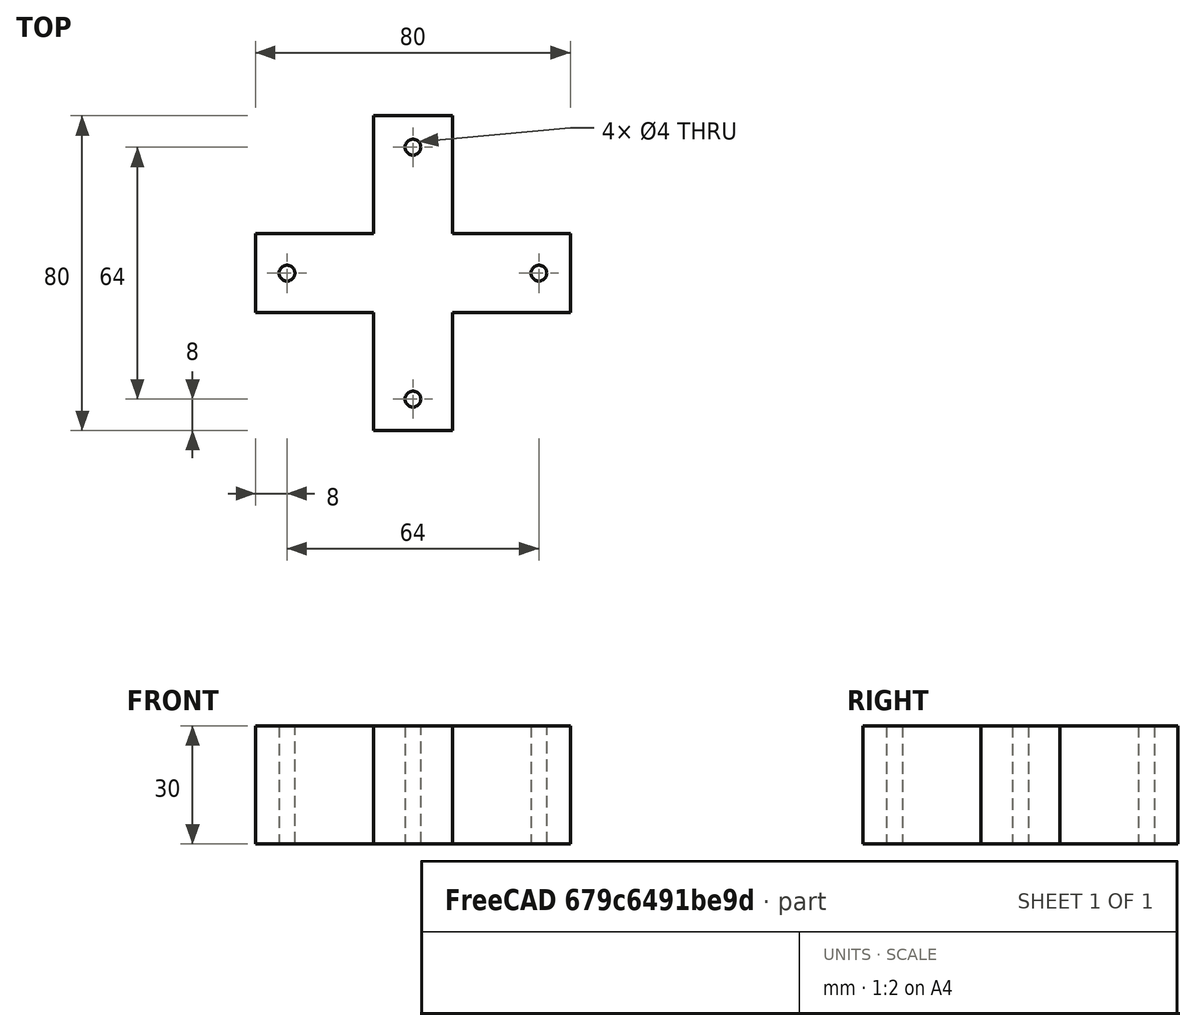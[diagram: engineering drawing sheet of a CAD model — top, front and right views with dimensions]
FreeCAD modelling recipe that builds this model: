
FCSTD DOCUMENT  (FreeCAD 0.21R33694 (Git))
Label: OJT1_T018_Creu
License: All rights reserved
LicenseURL: https://en.wikipedia.org/wiki/All_rights_reserved
objects: Sketcher::SketchObject×1, PartDesign::Pad×1, PartDesign::Body×1
note: 4 computed .brp shape members not serialized (recipe doc carries the construction recipe); baked Part::Feature solids carry a one-line shape summary decoded from their .brp

FEATURE [Sketcher::SketchObject] Sketch
  FullyConstrained = false
  MapMode = 5
  Support = -> [XY_Plane]
  sketch-geometry (16):
    g0: LineSegment StartX=-10 StartY=10 StartZ=0 EndX=-10 EndY=40 EndZ=0
    g1: LineSegment StartX=-10 StartY=40 StartZ=0 EndX=10 EndY=40 EndZ=0
    g2: LineSegment StartX=10 StartY=40 StartZ=0 EndX=10 EndY=10 EndZ=0
    g3: LineSegment StartX=10 StartY=10 StartZ=0 EndX=40 EndY=10 EndZ=0
    g4: LineSegment StartX=40 StartY=10 StartZ=0 EndX=40 EndY=-10 EndZ=0
    g5: LineSegment StartX=40 StartY=-10 StartZ=0 EndX=10 EndY=-10 EndZ=0
    g6: LineSegment StartX=10 StartY=-10 StartZ=0 EndX=10 EndY=-40 EndZ=0
    g7: LineSegment StartX=10 StartY=-40 StartZ=0 EndX=-10 EndY=-40 EndZ=0
    g8: LineSegment StartX=-10 StartY=-40 StartZ=0 EndX=-10 EndY=-10 EndZ=0
    g9: LineSegment StartX=-10 StartY=-10 StartZ=0 EndX=-40 EndY=-10 EndZ=0
    g10: LineSegment StartX=-40 StartY=-10 StartZ=0 EndX=-40 EndY=10 EndZ=0
    g11: LineSegment StartX=-40 StartY=10 StartZ=0 EndX=-10 EndY=10 EndZ=0
    g12: Circle CenterX=-32 CenterY=-3e-16 CenterZ=0 NormalX=0 NormalY=0 NormalZ=1 AngleXU=0 Radius=2
    g13: Circle CenterX=-4e-16 CenterY=-32 CenterZ=0 NormalX=0 NormalY=0 NormalZ=1 AngleXU=0 Radius=2
    g14: Circle CenterX=32 CenterY=-3e-16 CenterZ=0 NormalX=0 NormalY=0 NormalZ=1 AngleXU=0 Radius=2
    g15: Circle CenterX=-4e-16 CenterY=32 CenterZ=0 NormalX=0 NormalY=0 NormalZ=1 AngleXU=0 Radius=2
  constraints (39):
    c: Vertical(g0)
    c: Coincident(g0,g1)
    c: Horizontal(g1)
    c: Coincident(g1,g2)
    c: Vertical(g2)
    c: Coincident(g2,g3)
    c: Horizontal(g3)
    c: Coincident(g3,g4)
    c: Vertical(g4)
    c: Coincident(g4,g5)
    c: Horizontal(g5)
    c: Coincident(g5,g6)
    c: Vertical(g6)
    c: Coincident(g6,g7)
    c: Horizontal(g7)
    c: Coincident(g7,g8)
    c: Coincident(g8,g9)
    c: Horizontal(g9)
    c: Coincident(g9,g10)
    c: Vertical(g10)
    c: Coincident(g10,g11)
    c: Coincident(g11,g0)
    c: Symmetric(g3,g10,g-2)
    c: Symmetric(g8,g5,g-2)
    c: Symmetric(g0,g8,g-1)
    c: Symmetric(g7,g0,g-1)
    c: Symmetric(g0,g2,g-2)
    c: DistanceX(g1,g1) = 20
    c: DistanceY(g10,g10) = 20
    c: DistanceX(g11,g11) = 30
    c: DistanceY(g2,g2) = 30
    c: Equal(g12,g15)
    c: Equal(g15,g14)
    c: Equal(g14,g13)
    c: Diameter(g12) = 4
    c: Symmetric(g12,g14,g-2)
    c: Symmetric(g15,g13,g-1)
    c: DistanceY(g14,g3) = 10
    c: DistanceX(g14,g3) = 8
FEATURE [PartDesign::Pad] Pad
  Direction = (0,0,1)
  Length = 30
  Length2 = 10
  Profile = -> Sketch
  ReferenceAxis = -> Sketch [N_Axis]
  Type = 0
FEATURE [PartDesign::Body] Body
  Group = -> [Sketch,Pad]
  Origin = -> Origin
  Tip = -> Pad
